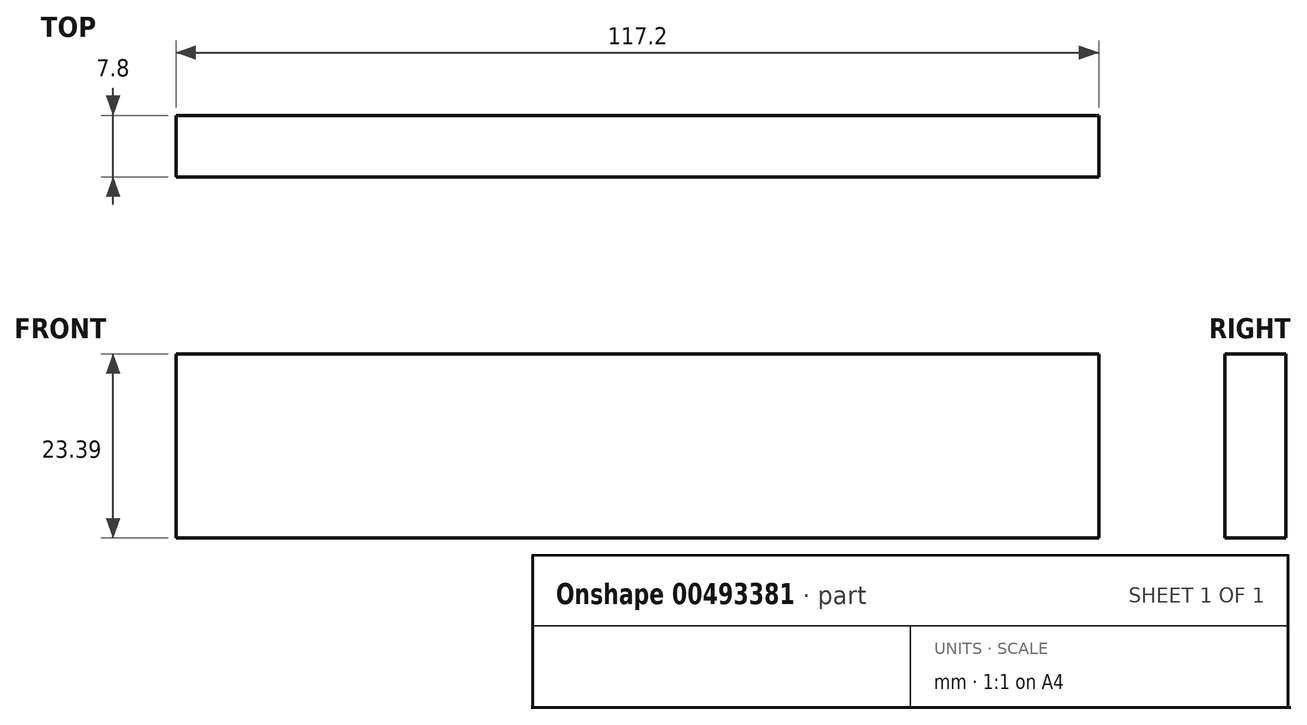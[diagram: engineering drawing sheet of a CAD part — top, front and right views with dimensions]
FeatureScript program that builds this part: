
annotation { "Feature Type Name" : "Feature", "Feature Type Description" : "" }
export const myFeature = defineFeature(function(context is Context, id is Id, definition is map)
    precondition{}
    {
        {
            var Q0;
            Q0=qCreatedBy(makeId("Front.planeOp"),FACE);
            var sketch = newSketch(context, id + "F0", { "sketchPlane" : qUnion([Q0])});
            skLineSegment(sketch, "E0.bottom", {"start": v(-56.27, -8.85) * mm, "end": v(60.93, -8.85) * mm});
            skLineSegment(sketch, "E0.top", {"start": v(-56.27, -32.24) * mm, "end": v(60.93, -32.24) * mm});
            skLineSegment(sketch, "E0.left", {"start": v(-56.27, -8.85) * mm, "end": v(-56.27, -32.24) * mm});
            skLineSegment(sketch, "E0.right", {"start": v(60.93, -8.85) * mm, "end": v(60.93, -32.24) * mm});
            skSolve(sketch);
        }
        {
            var Q0;
            Q0=makeQuery(id+"F0.imprint","IMPRINT",FACE,{"disambiguationData":[TD([[makeQuery(id+"F0.imprint","IMPRINT",EDGE,{"derivedFrom":sQuery(id+"F0.wireOp",EDGE,"E0.bottom")}),-1.0]])]});
            extrude(context, id + "F1", {"entities" : qUnion([Q0]), "endBound" : BoundingType.SYMMETRIC, "depth" : 7.8 * mm});
        }
    });
